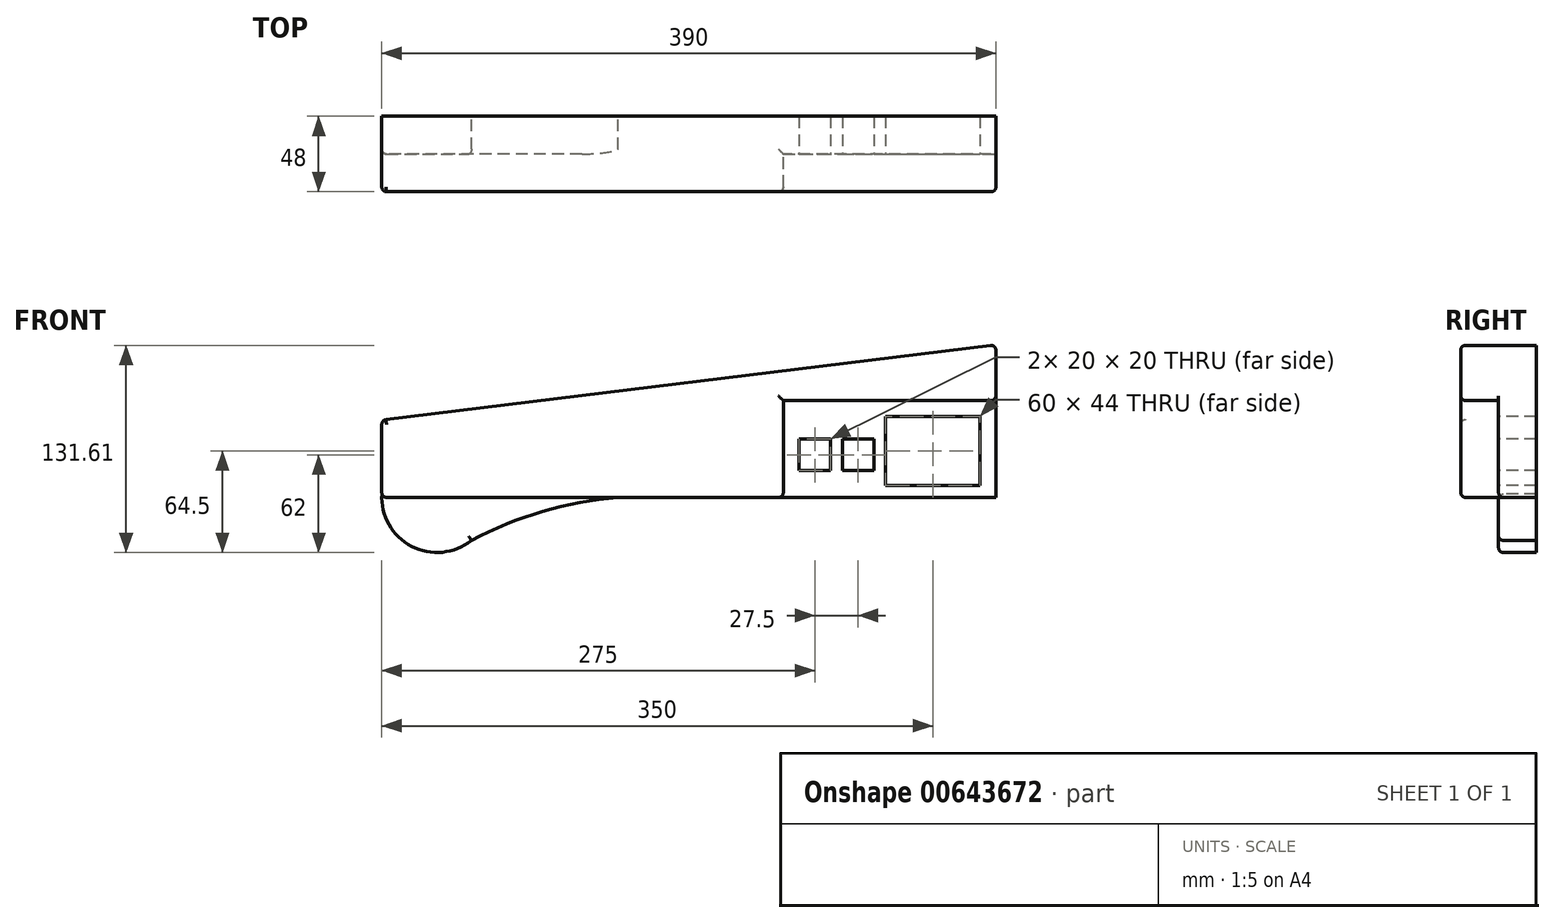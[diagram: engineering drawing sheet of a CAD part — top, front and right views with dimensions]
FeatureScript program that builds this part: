
annotation { "Feature Type Name" : "Feature", "Feature Type Description" : "" }
export const myFeature = defineFeature(function(context is Context, id is Id, definition is map)
    precondition{}
    {
        {
            var Q0;
            Q0=qCreatedBy(makeId("Front.planeOp"),FACE);
            var sketch = newSketch(context, id + "F0", { "sketchPlane" : qUnion([Q0])});
            skLineSegment(sketch, "E0.left", {"start": v(-195, 0) * mm, "end": v(-195, 49) * mm});
            skLineSegment(sketch, "E0.right", {"start": v(195, 0) * mm, "end": v(195, 97) * mm});
            skLineSegment(sketch, "E1", {"start": v(195, 97) * mm, "end": v(-195, 49) * mm});
            skArc(sketch, "E2", {"start": v(-195, 0) * mm, "mid": v(-175.12, -31.57) * mm, "end": v(-138.06, -27.27) * mm});
            skPoint(sketch, "E3.orphan", {"position": v(-125, 0) * mm});
            skArc(sketch, "E4.trimOffspring", {"start": v(-45, 0) * mm, "mid": v(-92.9, -8.98) * mm, "end": v(-138.06, -27.27) * mm});
            skLineSegment(sketch, "E5.trimOffspring", {"start": v(-45, 0) * mm, "end": v(195, 0) * mm});
            skSolve(sketch);
        }
        {
            var Q0;
            Q0=makeQuery(id+"F0.imprint","IMPRINT",FACE,{"disambiguationData":[TD([[makeQuery(id+"F0.imprint","IMPRINT",EDGE,{"derivedFrom":sQuery(id+"F0.wireOp",EDGE,"E0.left")}),-1.0]])]});
            extrude(context, id + "F1", {"entities" : qUnion([Q0]), "depth" : 24 * mm, "offsetDistance" : 25 * mm});
        }
        {
            var Q0;
            Q0=makeQuery(id+"F1.opExtrude","CAP_FACE",FACE,{"disambiguationData":[OSD([sQuery(id+"F0.wireOp",EDGE,"E0.left"),sQuery(id+"F0.wireOp",EDGE,"E0.right"),sQuery(id+"F0.wireOp",EDGE,"E1"),sQuery(id+"F0.wireOp",EDGE,"E2"),sQuery(id+"F0.wireOp",EDGE,"E4.trimOffspring"),sQuery(id+"F0.wireOp",EDGE,"E5.trimOffspring")])],"isStart":false});
            var sketch = newSketch(context, id + "F2", { "sketchPlane" : qUnion([Q0])});
            skLineSegment(sketch, "E6.bottom", {"start": v(195, 0) * mm, "end": v(-195, 0) * mm});
            skLineSegment(sketch, "E6.left", {"start": v(195, 0) * mm, "end": v(195, 97) * mm});
            skLineSegment(sketch, "E6.right", {"start": v(-195, 0) * mm, "end": v(-195, 49) * mm});
            skLineSegment(sketch, "E7", {"start": v(195, 61.5) * mm, "end": v(60, 61.5) * mm});
            skLineSegment(sketch, "E8", {"start": v(60, 61.5) * mm, "end": v(60, 0) * mm});
            skLineSegment(sketch, "E9", {"start": v(195, 97) * mm, "end": v(-195, 49) * mm});
            skPoint(sketch, "E10.orphan", {"position": v(-195, 97) * mm});
            skSolve(sketch);
        }
        {
            var Q0;
            {var subQ3=sQuery(id+"F2.wireOp",EDGE,"E6.right");Q0=makeQuery(id+"F2.imprint","IMPRINT",FACE,{"disambiguationData":[TD([[makeQuery(id+"F2.imprint","IMPRINT",EDGE,{"derivedFrom":subQ3}),-1.0]])]});}
            extrude(context, id + "F3", {"entities" : qUnion([Q0]), "operationType" : NewBodyOperationType.ADD, "depth" : 24 * mm, "offsetDistance" : 25 * mm});
        }
        {
            var Q0;
            {var subQ0=sQuery(id+"F0.wireOp",EDGE,"E5.trimOffspring");var subQ1=sQuery(id+"F0.wireOp",EDGE,"E0.right");Q0=makeQuery(id+"F3.boolean.opBoolean","SPLIT",FACE,{"disambiguationData":[TD([makeQuery(id+"F1.opExtrude","SWEPT_FACE",FACE,{"disambiguationData":[OSD([subQ1])]})])],"derivedFrom":makeQuery(id+"F1.opExtrude","CAP_FACE",FACE,{"disambiguationData":[OSD([sQuery(id+"F0.wireOp",EDGE,"E0.left"),subQ1,sQuery(id+"F0.wireOp",EDGE,"E1"),sQuery(id+"F0.wireOp",EDGE,"E2"),sQuery(id+"F0.wireOp",EDGE,"E4.trimOffspring"),subQ0])],"isStart":false})});}
            var sketch = newSketch(context, id + "F4", { "sketchPlane" : qUnion([Q0])});
            skLineSegment(sketch, "E11.bottom", {"start": v(70, 37) * mm, "end": v(90, 37) * mm});
            skLineSegment(sketch, "E11.top", {"start": v(70, 17) * mm, "end": v(90, 17) * mm});
            skLineSegment(sketch, "E11.left", {"start": v(70, 37) * mm, "end": v(70, 17) * mm});
            skLineSegment(sketch, "E11.right", {"start": v(90, 37) * mm, "end": v(90, 17) * mm});
            skLineSegment(sketch, "E12.bottom", {"start": v(97.5, 37) * mm, "end": v(117.5, 37) * mm});
            skLineSegment(sketch, "E12.top", {"start": v(97.5, 17) * mm, "end": v(117.5, 17) * mm});
            skLineSegment(sketch, "E12.left", {"start": v(97.5, 37) * mm, "end": v(97.5, 17) * mm});
            skLineSegment(sketch, "E12.right", {"start": v(117.5, 37) * mm, "end": v(117.5, 17) * mm});
            skLineSegment(sketch, "E13.bottom", {"start": v(125, 51.5) * mm, "end": v(185, 51.5) * mm});
            skLineSegment(sketch, "E13.top", {"start": v(125, 7.5) * mm, "end": v(185, 7.5) * mm});
            skLineSegment(sketch, "E13.left", {"start": v(125, 51.5) * mm, "end": v(125, 7.5) * mm});
            skLineSegment(sketch, "E13.right", {"start": v(185, 51.5) * mm, "end": v(185, 7.5) * mm});
            skSolve(sketch);
        }
        {
            var Q0;
            Q0 = qSketchRegion(id + "F4", true);
            extrude(context, id + "F5", {"entities" : qUnion([Q0]), "operationType" : NewBodyOperationType.REMOVE, "oppositeDirection" : true, "depth" : 24 * mm, "offsetDistance" : 25 * mm});
        }
        {
            var Q0;
            Q0=makeQuery(id+"F3.opExtrude","CAP_EDGE",EDGE,{"disambiguationData":[OSD([sQuery(id+"F2.wireOp",EDGE,"E7")])],"isStart":false});
            var Q1;
            Q1=makeQuery(id+"F3.opExtrude","CAP_EDGE",EDGE,{"disambiguationData":[OSD([sQuery(id+"F2.wireOp",EDGE,"E6.right")])],"isStart":false});
            var Q2;
            Q2=makeQuery(id+"F3.opExtrude","CAP_EDGE",EDGE,{"disambiguationData":[OSD([sQuery(id+"F2.wireOp",EDGE,"E8")])],"isStart":false});
            var Q3;
            Q3=makeQuery(id+"F1.opExtrude","CAP_EDGE",EDGE,{"disambiguationData":[OSD([sQuery(id+"F0.wireOp",EDGE,"E4.trimOffspring")])],"isStart":false});
            var Q4;
            Q4=makeQuery(id+"F3.opExtrude","CAP_EDGE",EDGE,{"disambiguationData":[OSD([sQuery(id+"F2.wireOp",EDGE,"E9")])],"isStart":false});
            var Q5;
            Q5=makeQuery(id+"F1.opExtrude","CAP_EDGE",EDGE,{"disambiguationData":[OSD([sQuery(id+"F0.wireOp",EDGE,"E2")])],"isStart":false});
            var Q6;
            Q6=makeQuery(id+"F3.opExtrude","CAP_EDGE",EDGE,{"disambiguationData":[OSD([sQuery(id+"F2.wireOp",EDGE,"E6.bottom")])],"isStart":false});
            fillet(context, id + "F6", {"entities" : qUnion([Q0, Q1, Q2, Q3, Q4, Q5, Q6]), "radius" : 3 * mm, "tangentPropagation" : true, "allowEdgeOverflow" : false});
        }
        {
            var Q0;
            Q0=makeQuery(id+"F3.opExtrude","CAP_EDGE",EDGE,{"disambiguationData":[OSD([sQuery(id+"F2.wireOp",EDGE,"E6.left")])],"isStart":false});
            fillet(context, id + "F7", {"entities" : qUnion([Q0]), "radius" : 3 * mm, "tangentPropagation" : true, "allowEdgeOverflow" : false});
        }
        {
            var Q0;
            Q0=makeQuery(id+"F1.opExtrude","CAP_EDGE",EDGE,{"disambiguationData":[OSD([sQuery(id+"F0.wireOp",EDGE,"E5.trimOffspring")])],"isStart":false});
            var Q1;
            Q1=makeQuery(id+"F3.opExtrude","SWEPT_EDGE",EDGE,{"disambiguationData":[OSD([sQuery(id+"F2.wireOp",EDGE,"E6.bottom"),sQuery(id+"F2.wireOp",EDGE,"E8")])]});
            fillet(context, id + "F8", {"entities" : qUnion([Q0, Q1]), "radius" : 3 * mm, "tangentPropagation" : true, "allowEdgeOverflow" : false});
        }
        {
            var Q0;
            Q0=makeQuery(id+"F3.boolean.opBoolean","MERGE",EDGE,{"derivedFrom":[makeQuery(id+"F1.opExtrude","SWEPT_EDGE",EDGE,{"disambiguationData":[OSD([sQuery(id+"F0.wireOp",EDGE,"E0.left"),sQuery(id+"F0.wireOp",EDGE,"E1")])]}),makeQuery(id+"F3.opExtrude","SWEPT_EDGE",EDGE,{"disambiguationData":[OSD([sQuery(id+"F2.wireOp",EDGE,"E6.right"),sQuery(id+"F2.wireOp",EDGE,"E9")])]})]});
            fillet(context, id + "F9", {"entities" : qUnion([Q0]), "radius" : 3 * mm, "tangentPropagation" : true, "allowEdgeOverflow" : false});
        }
        {
            var Q0;
            Q0=makeQuery(id+"F3.opExtrude","SWEPT_EDGE",EDGE,{"disambiguationData":[OSD([sQuery(id+"F0.wireOp",EDGE,"E2"),sQuery(id+"F2.wireOp",EDGE,"E6.bottom"),sQuery(id+"F2.wireOp",EDGE,"E6.right")])]});
            fillet(context, id + "F10", {"entities" : qUnion([Q0]), "radius" : 3 * mm, "tangentPropagation" : true, "allowEdgeOverflow" : false});
        }
    });
